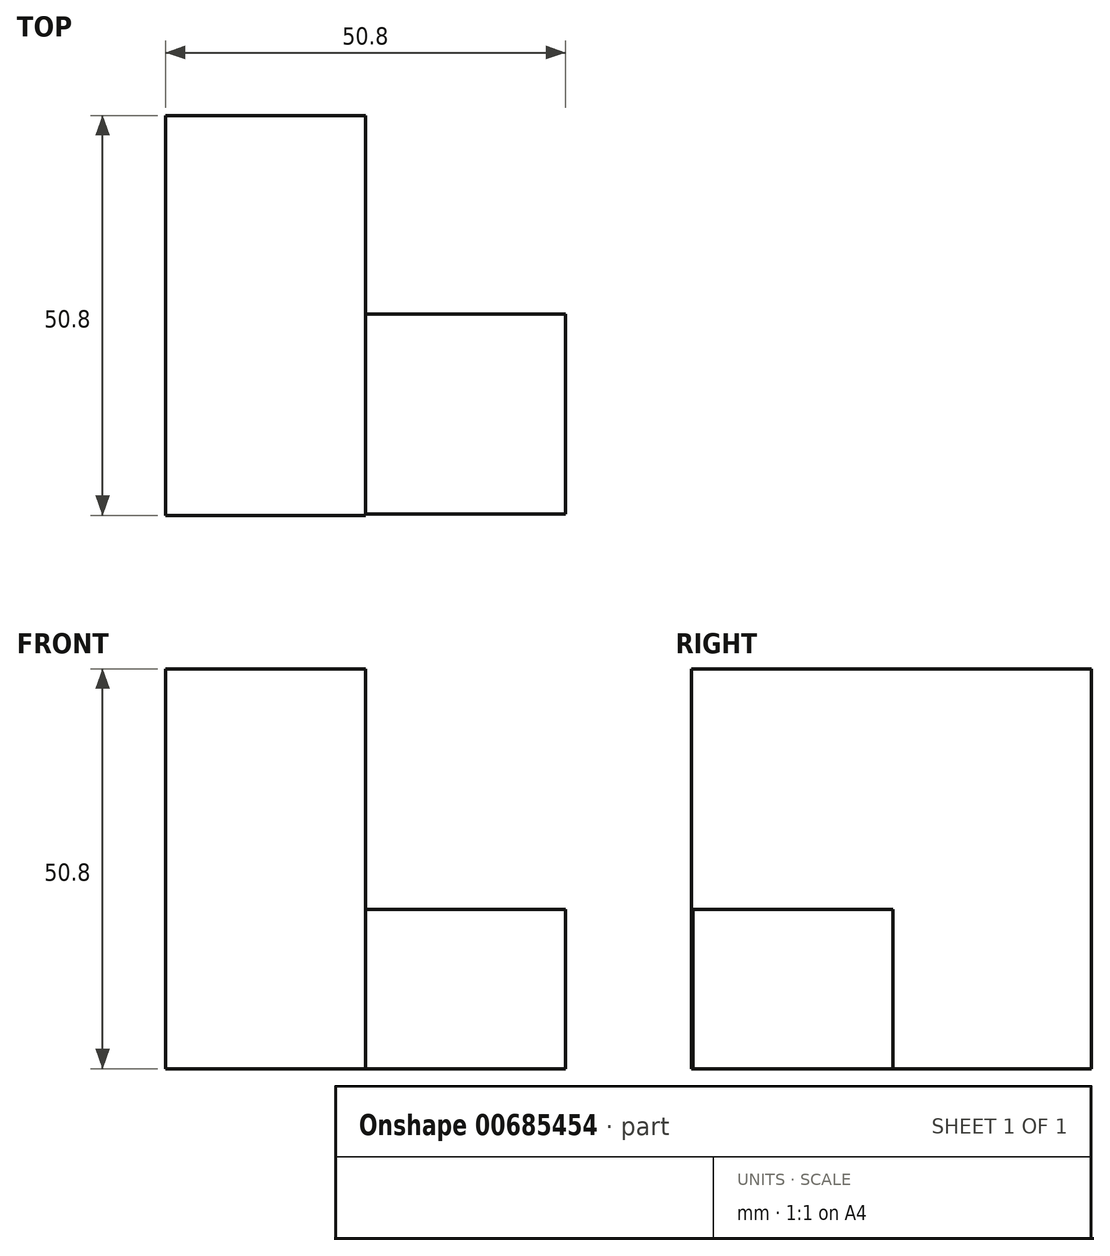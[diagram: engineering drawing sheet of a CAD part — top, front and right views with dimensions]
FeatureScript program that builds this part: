
annotation { "Feature Type Name" : "Feature", "Feature Type Description" : "" }
export const myFeature = defineFeature(function(context is Context, id is Id, definition is map)
    precondition{}
    {
        {
            var Q0;
            Q0=qCreatedBy(makeId("Front.planeOp"),FACE);
            var sketch = newSketch(context, id + "F0", { "sketchPlane" : qUnion([Q0])});
            skLineSegment(sketch, "E0.bottom", {"start": v(0, 0) * mm, "end": v(-25.4, 0) * mm});
            skLineSegment(sketch, "E0.top", {"start": v(0, 50.8) * mm, "end": v(-25.4, 50.8) * mm});
            skLineSegment(sketch, "E0.left", {"start": v(0, 0) * mm, "end": v(0, 50.8) * mm});
            skLineSegment(sketch, "E0.right", {"start": v(-25.4, 0) * mm, "end": v(-25.4, 50.8) * mm});
            skSolve(sketch);
        }
        {
            var Q0;
            Q0=makeQuery(id+"F0.imprint","IMPRINT",FACE,{"disambiguationData":[TD([[makeQuery(id+"F0.imprint","IMPRINT",EDGE,{"derivedFrom":sQuery(id+"F0.wireOp",EDGE,"E0.bottom")}),-1.0]])]});
            extrude(context, id + "F1", {"entities" : qUnion([Q0]), "depth" : 50.8 * mm, "offsetDistance" : 25.4 * mm});
        }
        {
            var Q0;
            Q0=qCreatedBy(makeId("Right.planeOp"),FACE);
            var sketch = newSketch(context, id + "F2", { "sketchPlane" : qUnion([Q0])});
            skLineSegment(sketch, "E1.bottom", {"start": v(-50.63, 0) * mm, "end": v(-25.23, 0) * mm});
            skLineSegment(sketch, "E1.top", {"start": v(-50.63, 20.2) * mm, "end": v(-25.23, 20.2) * mm});
            skLineSegment(sketch, "E1.left", {"start": v(-50.63, 0) * mm, "end": v(-50.63, 20.2) * mm});
            skLineSegment(sketch, "E1.right", {"start": v(-25.23, 0) * mm, "end": v(-25.23, 20.2) * mm});
            skSolve(sketch);
        }
        {
            var Q0;
            Q0 = qSketchRegion(id + "F2", true);
            extrude(context, id + "F3", {"entities" : qUnion([Q0]), "operationType" : NewBodyOperationType.ADD, "depth" : 25.4 * mm, "offsetDistance" : 25.4 * mm});
        }
    });
